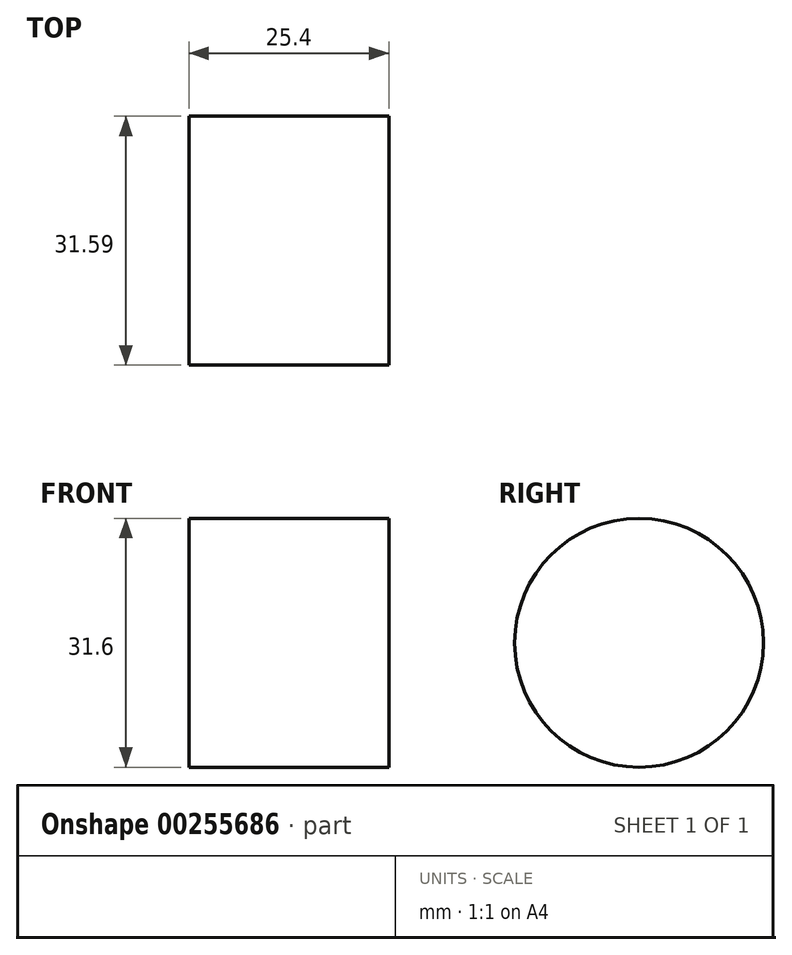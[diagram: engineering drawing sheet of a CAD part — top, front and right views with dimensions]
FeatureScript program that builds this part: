
annotation { "Feature Type Name" : "Feature", "Feature Type Description" : "" }
export const myFeature = defineFeature(function(context is Context, id is Id, definition is map)
    precondition{}
    {
        {
            var Q0;
            Q0=qCreatedBy(makeId("Right.planeOp"),FACE);
            var sketch = newSketch(context, id + "F0", { "sketchPlane" : qUnion([Q0])});
            skCircle(sketch, "E0", {"center": v(-17.5, 7.68) * mm, "radius": 15.8 * mm});
            skSolve(sketch);
        }
        {
            var Q0;
            Q0=makeQuery(id+"F0.imprint","IMPRINT",FACE,{"disambiguationData":[TD([[makeQuery(id+"F0.imprint","IMPRINT",EDGE,{"derivedFrom":sQuery(id+"F0.wireOp",EDGE,"E0")}),1.0]])]});
            extrude(context, id + "F1", {"entities" : qUnion([Q0]), "depth" : 25.4 * mm});
        }
    });
